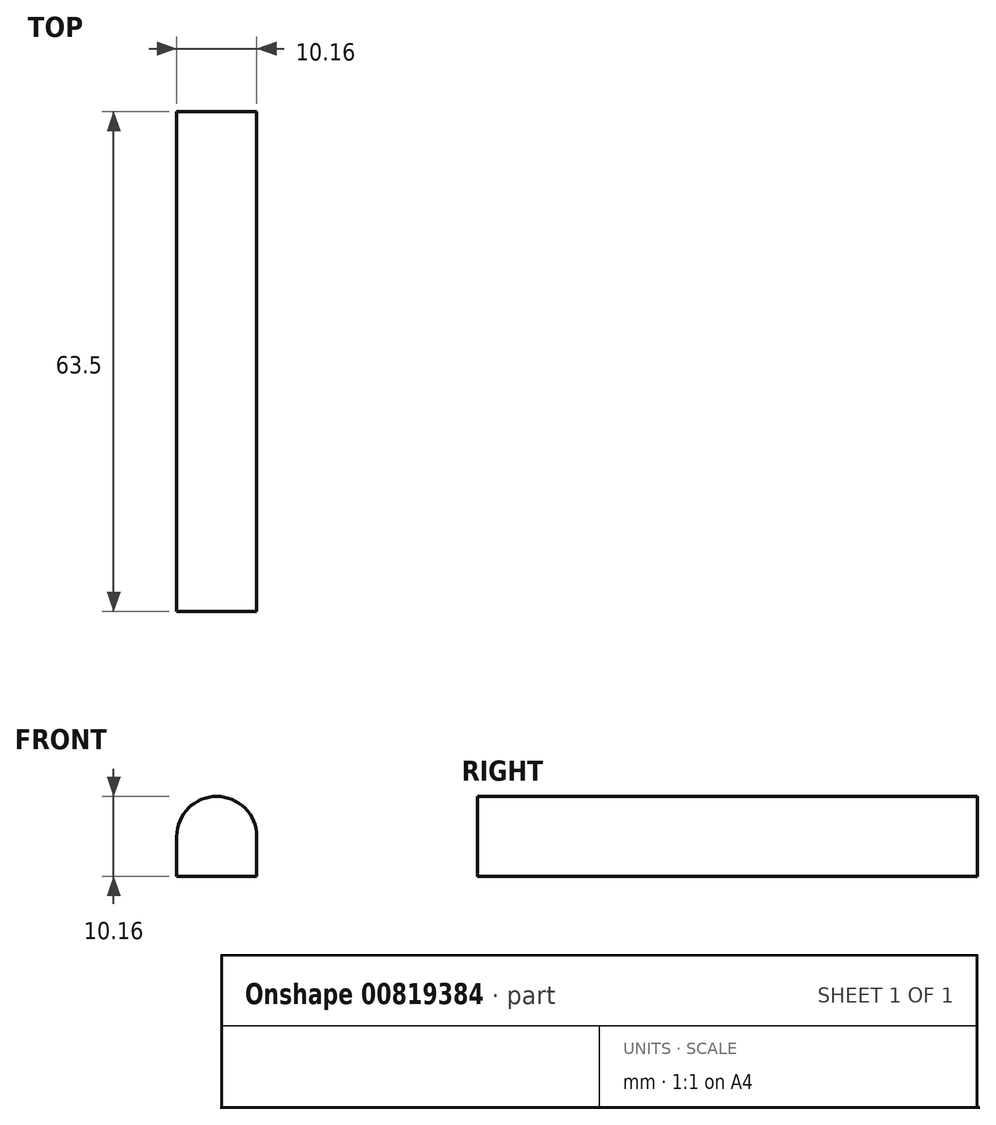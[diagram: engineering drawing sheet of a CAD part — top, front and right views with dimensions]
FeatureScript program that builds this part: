
annotation { "Feature Type Name" : "Feature", "Feature Type Description" : "" }
export const myFeature = defineFeature(function(context is Context, id is Id, definition is map)
    precondition{}
    {
        {
            var Q0;
            Q0=qCreatedBy(makeId("Front.planeOp"),FACE);
            var sketch = newSketch(context, id + "F0", { "sketchPlane" : qUnion([Q0])});
            skLineSegment(sketch, "E0", {"start": v(0, 5.08) * mm, "end": v(0, 0) * mm});
            skLineSegment(sketch, "E1", {"start": v(0, 0) * mm, "end": v(10.16, 0) * mm});
            skLineSegment(sketch, "E2", {"start": v(10.16, 0) * mm, "end": v(10.16, 5.08) * mm});
            skArc(sketch, "E3", {"start": v(10.16, 5.08) * mm, "mid": v(5.08, 10.16) * mm, "end": v(0, 5.08) * mm});
            skSolve(sketch);
        }
        {
            var Q0;
            Q0 = qSketchRegion(id + "F0", true);
            extrude(context, id + "F1", {"entities" : qUnion([Q0]), "depth" : 63.5 * mm, "offsetDistance" : 25.4 * mm});
        }
    });
